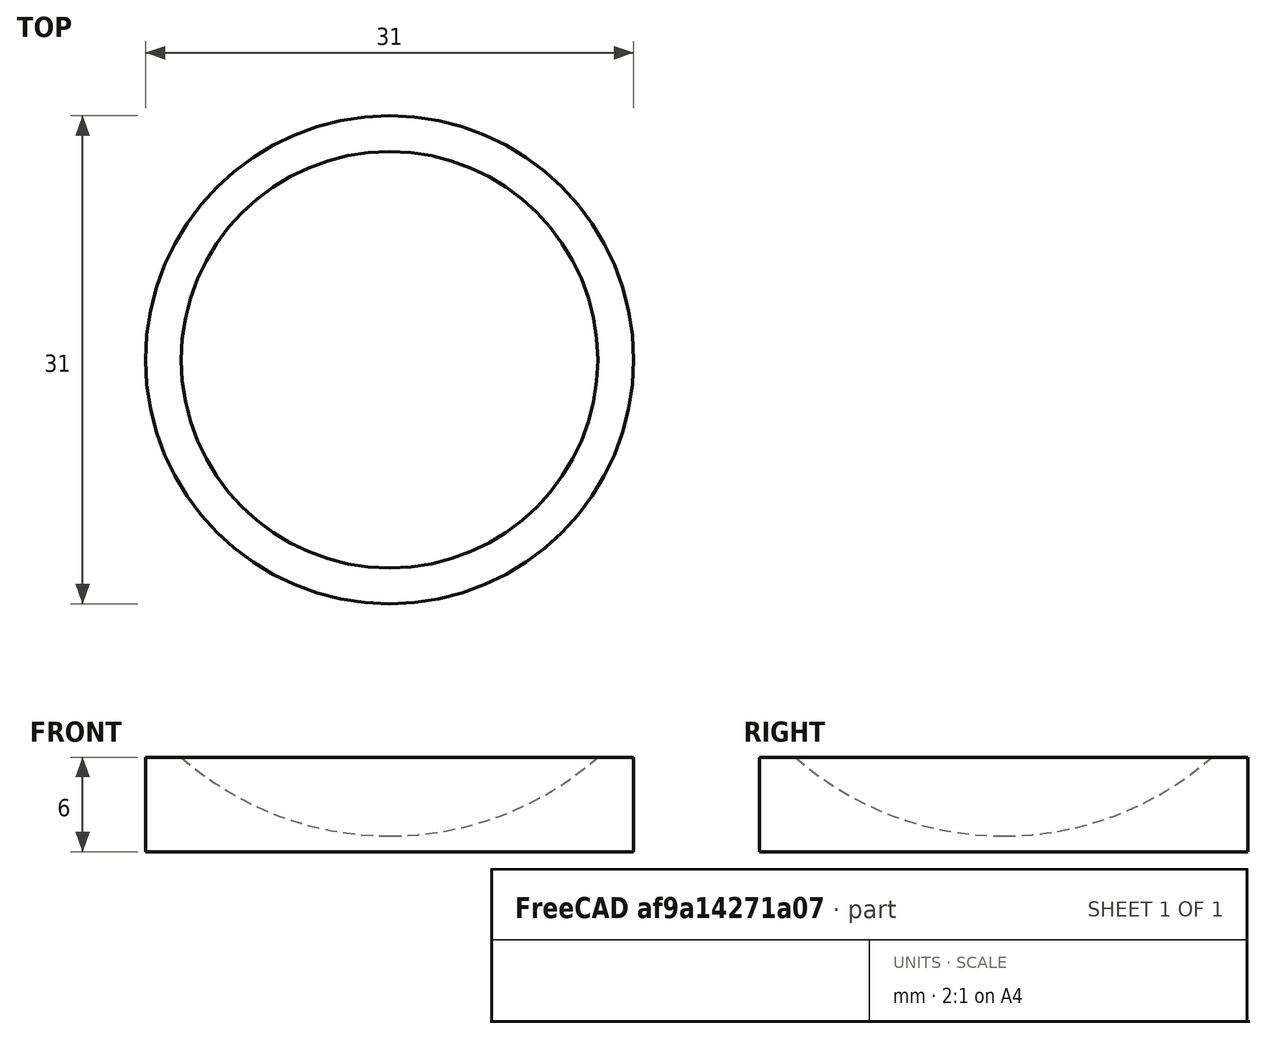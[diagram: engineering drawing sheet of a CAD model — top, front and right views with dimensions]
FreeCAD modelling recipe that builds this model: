
FCSTD DOCUMENT  (FreeCAD 0.20R29603 (Git))
Label: workbench_pillar
License: All rights reserved
LicenseURL: http://en.wikipedia.org/wiki/All_rights_reserved
objects: Sketcher::SketchObject×1, PartDesign::Pad×1, PartDesign::Body×1, Part::Sphere×1, Part::Cut×1
note: 6 computed .brp shape members not serialized (recipe doc carries the construction recipe); baked Part::Feature solids carry a one-line shape summary decoded from their .brp

FEATURE [Sketcher::SketchObject] Sketch
  FullyConstrained = true
  MapMode = 5
  Support = -> [XY_Plane]
  sketch-geometry (1):
    g0: Circle CenterX=0 CenterY=0 CenterZ=0 NormalX=0 NormalY=0 NormalZ=1 AngleXU=0 Radius=15.5
  constraints (2):
    c: Coincident(g0,g-1)
    c: Diameter(g0) = 31
FEATURE [PartDesign::Pad] Pad
  Direction = (0,0,1)
  Length = 6
  Length2 = 10
  Profile = -> Sketch
  ReferenceAxis = -> Sketch [N_Axis]
  Type = 0
FEATURE [PartDesign::Body] Body
  Group = -> [Sketch,Pad]
  Origin = -> Origin
  Tip = -> Pad
FEATURE [Part::Sphere] Sphere  label="Сфера"
  Angle1 = -90
  Angle2 = 90
  Angle3 = 360
  AttacherType = Attacher::AttachEngine3D
  Placement = pos=(0,0,21) rot=(0,0,1;0rad)
  Radius = 20
FEATURE [Part::Cut] Cut
  Base = -> Body
  Tool = -> Sphere
